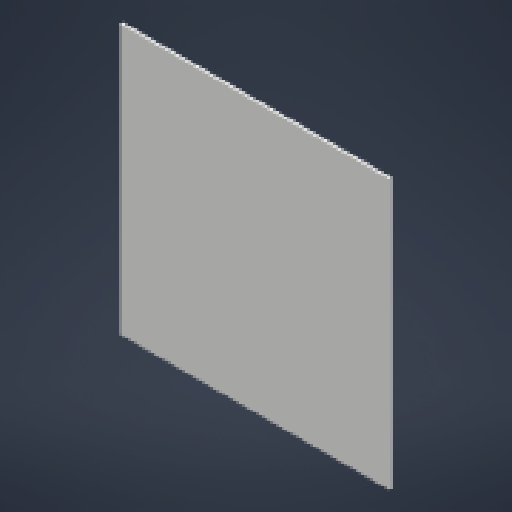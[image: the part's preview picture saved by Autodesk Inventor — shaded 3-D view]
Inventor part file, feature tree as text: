
AUTODESK INVENTOR PART (.ipt)
format: ipt  version: 2024 (Build 280153000, 153)  size: 108,544 bytes
history: native  units: mm
features: other x2, extrude x1, sketch x1
ambient origin geometry x8: Origin, YZ Plane, XZ Plane, XY Plane, X Axis, Y Axis, Z Axis, Center Point
bodies: Body1 (feature_tree)
feature tree (4):
  other  "솔리드1"
  extrude  "돌출1"  Depth=500.0mm
  sketch  "스케치1"
  other  "Finish1"
